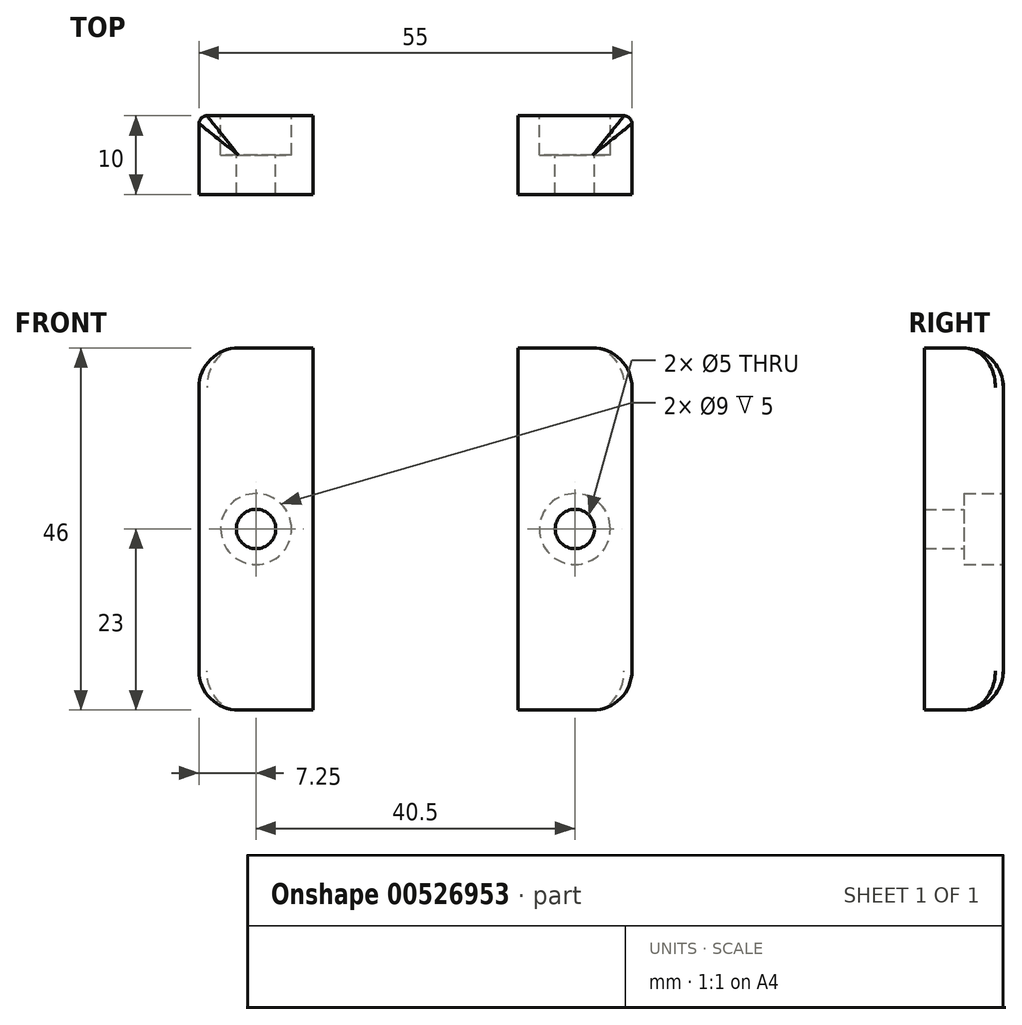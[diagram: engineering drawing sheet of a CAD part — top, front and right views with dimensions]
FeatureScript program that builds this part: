
annotation { "Feature Type Name" : "Feature", "Feature Type Description" : "" }
export const myFeature = defineFeature(function(context is Context, id is Id, definition is map)
    precondition{}
    {
        {
            var Q0;
            Q0=qCreatedBy(makeId("Top.planeOp"),FACE);
            var sketch = newSketch(context, id + "F0", { "sketchPlane" : qUnion([Q0])});
            skArc(sketch, "E0", {"start": v(-13, 0) * mm, "mid": v(0, 13) * mm, "end": v(13, 0) * mm});
            skLineSegment(sketch, "E1", {"start": v(-13, 0) * mm, "end": v(-27.5, 0) * mm});
            skArc(sketch, "E2", {"start": v(-27.5, 0) * mm, "mid": v(0, 27.5) * mm, "end": v(27.5, 0) * mm});
            skLineSegment(sketch, "E3", {"start": v(13, 0) * mm, "end": v(27.5, 0) * mm});
            skPoint(sketch, "E4", {"position": v(-20.25, 0) * mm});
            skPoint(sketch, "E5", {"position": v(20.25, 0) * mm});
            skLineSegment(sketch, "E6", {"start": v(-27.5, 0) * mm, "end": v(-27.5, 10) * mm});
            skLineSegment(sketch, "E7", {"start": v(-27.5, 10) * mm, "end": v(-13, 10) * mm});
            skLineSegment(sketch, "E8", {"start": v(-13, 10) * mm, "end": v(-13, 0) * mm});
            skLineSegment(sketch, "E9", {"start": v(27.5, 0) * mm, "end": v(27.5, 10) * mm});
            skLineSegment(sketch, "E10", {"start": v(27.5, 10) * mm, "end": v(13, 10) * mm});
            skLineSegment(sketch, "E11", {"start": v(13, 10) * mm, "end": v(13, 0) * mm});
            skPoint(sketch, "E12", {"position": v(-20.25, 10) * mm});
            skPoint(sketch, "E13", {"position": v(20.25, 10) * mm});
            skSolve(sketch);
        }
        {
            var Q0;
            Q0=makeQuery(id+"F0.imprint","IMPRINT",FACE,{"disambiguationData":[TD([[makeQuery(id+"F0.imprint","IMPRINT",EDGE,{"derivedFrom":sQuery(id+"F0.wireOp",EDGE,"E0")}),1.0]])]});
            var Q1;
            {var subQ0=sQuery(id+"F0.wireOp",EDGE,"E1");Q1=makeQuery(id+"F0.imprint","IMPRINT",FACE,{"disambiguationData":[TD([[makeQuery(id+"F0.imprint","IMPRINT",EDGE,{"derivedFrom":subQ0}),-1.0]])]});}
            var Q2;
            {var subQ0=sQuery(id+"F0.wireOp",EDGE,"E3");Q2=makeQuery(id+"F0.imprint","IMPRINT",FACE,{"disambiguationData":[TD([[makeQuery(id+"F0.imprint","IMPRINT",EDGE,{"derivedFrom":subQ0}),1.0]])]});}
            var Q3;
            {var subQ0=sQuery(id+"F0.wireOp",EDGE,"E6");Q3=makeQuery(id+"F0.imprint","IMPRINT",FACE,{"disambiguationData":[TD([[makeQuery(id+"F0.imprint","IMPRINT",EDGE,{"derivedFrom":subQ0}),-1.0]])]});}
            var Q4;
            {var subQ0=sQuery(id+"F0.wireOp",EDGE,"E9");Q4=makeQuery(id+"F0.imprint","IMPRINT",FACE,{"disambiguationData":[TD([[makeQuery(id+"F0.imprint","IMPRINT",EDGE,{"derivedFrom":subQ0}),1.0]])]});}
            extrude(context, id + "F1", {"entities" : qUnion([Q0, Q1, Q2, Q3, Q4]), "depth" : 46 * mm, "offsetDistance" : 25 * mm, "symmetric" : true});
        }
        {
            var Q0;
            Q0=qCreatedBy(makeId("Front.planeOp"),FACE);
            cPlane(context, id + "F2", {"entities" : qUnion([Q0]), "cplaneType" : CPlaneType.OFFSET, "offset" : 10 * mm, "oppositeDirection" : true, "width" : 150 * mm, "height" : 150 * mm});
        }
        {
            var Q0;
            Q0=qCreatedBy(id+"F2.planeOp",FACE);
            var sketch = newSketch(context, id + "F3", { "sketchPlane" : qUnion([Q0])});
            skPoint(sketch, "E14", {"position": v(-20.25, 0) * mm});
            skPoint(sketch, "E15", {"position": v(20.25, 0) * mm});
            skSolve(sketch);
        }
        {
            var Q0;
            Q0=sQuery(id+"F3.wireOp",VERTEX,"E15");
            var Q1;
            Q1=sQuery(id+"F3.wireOp",VERTEX,"E14");
            var Q2;
            Q2=makeQuery(id+"F1.opExtrude","SWEPT_BODY",BODY,{"disambiguationData":[OSD([sQuery(id+"F0.wireOp",EDGE,"E0"),sQuery(id+"F0.wireOp",EDGE,"E1"),sQuery(id+"F0.wireOp",EDGE,"E2"),sQuery(id+"F0.wireOp",EDGE,"E3"),sQuery(id+"F0.wireOp",EDGE,"E6"),sQuery(id+"F0.wireOp",EDGE,"E7"),sQuery(id+"F0.wireOp",EDGE,"E9"),sQuery(id+"F0.wireOp",EDGE,"E10")])]});
            hole(context, id + "F4", {"style" : HoleStyle.SIMPLE, "endStyle" : HoleEndStyle.BLIND, "holeDiameter" : 9 * mm, "holeDepth" : 15 * mm, "isTappedThrough" : true, "tappedDepth" : 12 * mm, "tapClearance" : 3, "startFromSketch" : true, "locations" : qUnion([Q0, Q1]), "scope" : qUnion([Q2])});
        }
        {
            var Q0;
            Q0=sQuery(id+"F3.wireOp",VERTEX,"E14");
            var Q1;
            Q1=sQuery(id+"F3.wireOp",VERTEX,"E15");
            var Q2;
            Q2=makeQuery(id+"F1.opExtrude","SWEPT_BODY",BODY,{"disambiguationData":[OSD([sQuery(id+"F0.wireOp",EDGE,"E0"),sQuery(id+"F0.wireOp",EDGE,"E1"),sQuery(id+"F0.wireOp",EDGE,"E2"),sQuery(id+"F0.wireOp",EDGE,"E3"),sQuery(id+"F0.wireOp",EDGE,"E6"),sQuery(id+"F0.wireOp",EDGE,"E7"),sQuery(id+"F0.wireOp",EDGE,"E9"),sQuery(id+"F0.wireOp",EDGE,"E10")])]});
            hole(context, id + "F5", {"style" : HoleStyle.C_BORE, "endStyle" : HoleEndStyle.BLIND, "oppositeDirection" : true, "holeDiameter" : 5 * mm, "cBoreDiameter" : 9 * mm, "cBoreDepth" : 5 * mm, "holeDepth" : 15 * mm, "isTappedThrough" : true, "tappedDepth" : 12 * mm, "tapClearance" : 3, "locations" : qUnion([Q0, Q1]), "scope" : qUnion([Q2])});
        }
        {
            var Q0;
            Q0=makeQuery(id+"F1.opExtrude","CAP_EDGE",EDGE,{"disambiguationData":[OSD([sQuery(id+"F0.wireOp",EDGE,"E9")])],"isStart":true});
            var Q1;
            Q1=makeQuery(id+"F1.opExtrude","CAP_EDGE",EDGE,{"disambiguationData":[OSD([sQuery(id+"F0.wireOp",EDGE,"E6")])],"isStart":true});
            var Q2;
            Q2=makeQuery(id+"F1.opExtrude","CAP_EDGE",EDGE,{"disambiguationData":[OSD([sQuery(id+"F0.wireOp",EDGE,"E7")])],"isStart":true});
            var Q3;
            Q3=makeQuery(id+"F1.opExtrude","CAP_EDGE",EDGE,{"disambiguationData":[OSD([sQuery(id+"F0.wireOp",EDGE,"E2")])],"isStart":true});
            var Q4;
            Q4=makeQuery(id+"F1.opExtrude","CAP_EDGE",EDGE,{"disambiguationData":[OSD([sQuery(id+"F0.wireOp",EDGE,"E10")])],"isStart":true});
            fillet(context, id + "F6", {"entities" : qUnion([Q0, Q1, Q2, Q3, Q4]), "radius" : 5 * mm, "tangentPropagation" : true, "allowEdgeOverflow" : false});
        }
        {
            var Q0;
            Q0=makeQuery(id+"F1.opExtrude","CAP_EDGE",EDGE,{"disambiguationData":[OSD([sQuery(id+"F0.wireOp",EDGE,"E2")])],"isStart":false});
            var Q1;
            Q1=makeQuery(id+"F1.opExtrude","CAP_EDGE",EDGE,{"disambiguationData":[OSD([sQuery(id+"F0.wireOp",EDGE,"E10")])],"isStart":false});
            var Q2;
            Q2=makeQuery(id+"F1.opExtrude","CAP_EDGE",EDGE,{"disambiguationData":[OSD([sQuery(id+"F0.wireOp",EDGE,"E7")])],"isStart":false});
            var Q3;
            Q3=makeQuery(id+"F1.opExtrude","CAP_EDGE",EDGE,{"disambiguationData":[OSD([sQuery(id+"F0.wireOp",EDGE,"E6")])],"isStart":false});
            var Q4;
            Q4=makeQuery(id+"F1.opExtrude","CAP_EDGE",EDGE,{"disambiguationData":[OSD([sQuery(id+"F0.wireOp",EDGE,"E9")])],"isStart":false});
            fillet(context, id + "F7", {"entities" : qUnion([Q0, Q1, Q2, Q3, Q4]), "radius" : 5 * mm, "tangentPropagation" : true, "allowEdgeOverflow" : false});
        }
        {
            var Q0;
            Q0=makeQuery(id+"F1.opExtrude","SWEPT_EDGE",EDGE,{"disambiguationData":[OSD([sQuery(id+"F0.wireOp",EDGE,"E9"),sQuery(id+"F0.wireOp",EDGE,"E10")])]});
            fillet(context, id + "F8", {"entities" : qUnion([Q0]), "radius" : 1 * mm, "tangentPropagation" : true, "allowEdgeOverflow" : false});
        }
        {
            var Q0;
            Q0=makeQuery(id+"F1.opExtrude","SWEPT_EDGE",EDGE,{"disambiguationData":[OSD([sQuery(id+"F0.wireOp",EDGE,"E6"),sQuery(id+"F0.wireOp",EDGE,"E7")])]});
            fillet(context, id + "F9", {"entities" : qUnion([Q0]), "radius" : 1 * mm, "tangentPropagation" : true, "allowEdgeOverflow" : false});
        }
    });
